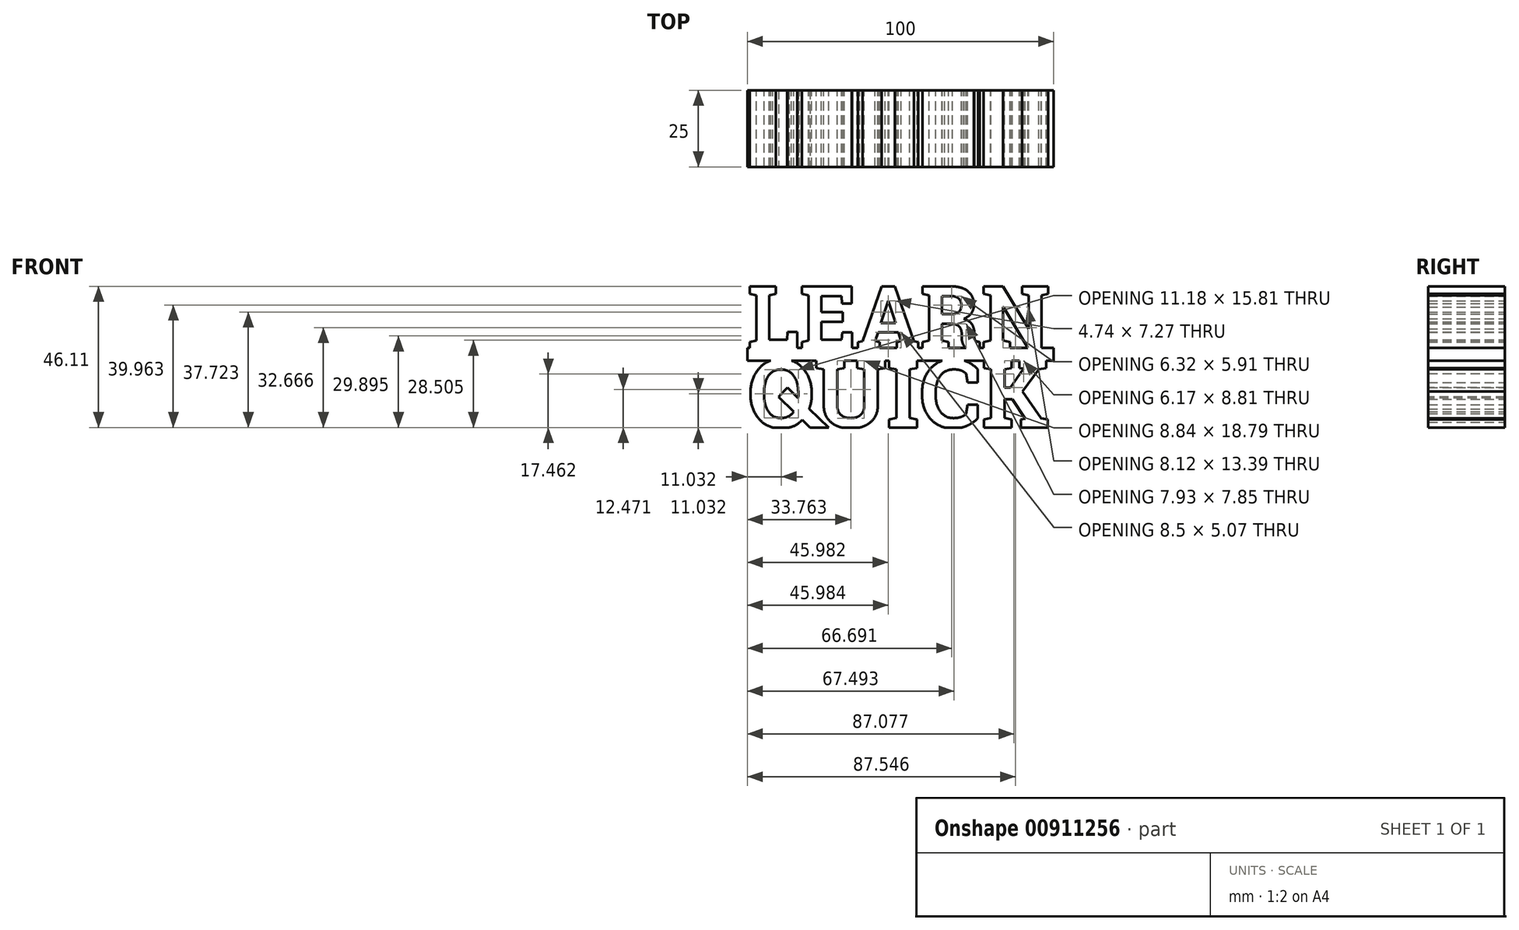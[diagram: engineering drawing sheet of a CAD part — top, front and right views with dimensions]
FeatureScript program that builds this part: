
annotation { "Feature Type Name" : "Feature", "Feature Type Description" : "" }
export const myFeature = defineFeature(function(context is Context, id is Id, definition is map)
    precondition{}
    {
        {
            var Q0;
            Q0=qCreatedBy(makeId("Front.planeOp"),FACE);
            var sketch = newSketch(context, id + "F0", { "sketchPlane" : qUnion([Q0])});
            skText(sketch, "E0", { "text": "LEARN", "fontName": "RobotoSlab-Bold.ttf"});
            skText(sketch, "E1", { "text": "QUICK", "fontName": "RobotoSlab-Bold.ttf"});
            skPoint(sketch, "E2", {"position": v(-50, 0.5) * mm});
            skPoint(sketch, "E3", {"position": v(50, -3.6) * mm});
            skLineSegment(sketch, "E4.bottom", {"start": v(-50, 0.5) * mm, "end": v(50, 0.5) * mm});
            skLineSegment(sketch, "E4.top", {"start": v(-50, -3.6) * mm, "end": v(50, -3.6) * mm});
            skLineSegment(sketch, "E4.left", {"start": v(-50, 0.5) * mm, "end": v(-50, -3.6) * mm});
            skLineSegment(sketch, "E4.right", {"start": v(50, 0.5) * mm, "end": v(50, -3.6) * mm});
            const initialGuessF0  = {"E0": [-0.05, 0, 1, 0, 0.0209], "E1": [-0.05, -0.02547, 1, 0, 0.02236]};
            skSetInitialGuess(sketch, initialGuessF0);
            skSolve(sketch);
        }
        {
            var Q0;
            Q0 = qSketchRegion(id + "F0", true);
            extrude(context, id + "F1", {"entities" : qUnion([Q0]), "depth" : 25 * mm, "offsetDistance" : 25 * mm});
        }
        {
            var Q0;
            Q0=makeQuery(id+"F1.opExtrude","CAP_FACE",FACE,{"disambiguationData":[OSD([sQuery(id+"F0.wireOp",EDGE,"E0.sketch_text.stroke-0"),sQuery(id+"F0.wireOp",EDGE,"E0.sketch_text.stroke-1"),sQuery(id+"F0.wireOp",EDGE,"E0.sketch_text.stroke-2"),sQuery(id+"F0.wireOp",EDGE,"E0.sketch_text.stroke-3"),sQuery(id+"F0.wireOp",EDGE,"E0.sketch_text.stroke-4"),sQuery(id+"F0.wireOp",EDGE,"E0.sketch_text.stroke-5"),sQuery(id+"F0.wireOp",EDGE,"E0.sketch_text.stroke-6"),sQuery(id+"F0.wireOp",EDGE,"E0.sketch_text.stroke-7"),sQuery(id+"F0.wireOp",EDGE,"E0.sketch_text.stroke-8"),sQuery(id+"F0.wireOp",EDGE,"E0.sketch_text.stroke-9"),sQuery(id+"F0.wireOp",EDGE,"E0.sketch_text.stroke-10"),sQuery(id+"F0.wireOp",EDGE,"E0.sketch_text.stroke-11"),sQuery(id+"F0.wireOp",EDGE,"E0.sketch_text.stroke-12"),sQuery(id+"F0.wireOp",EDGE,"E0.sketch_text.stroke-13"),sQuery(id+"F0.wireOp",EDGE,"E0.sketch_text.stroke-14"),sQuery(id+"F0.wireOp",EDGE,"E0.sketch_text.stroke-15"),sQuery(id+"F0.wireOp",EDGE,"E1.sketch_text.stroke-0"),sQuery(id+"F0.wireOp",EDGE,"E1.sketch_text.stroke-1"),sQuery(id+"F0.wireOp",EDGE,"E1.sketch_text.stroke-2"),sQuery(id+"F0.wireOp",EDGE,"E1.sketch_text.stroke-3"),sQuery(id+"F0.wireOp",EDGE,"E1.sketch_text.stroke-4"),sQuery(id+"F0.wireOp",EDGE,"E1.sketch_text.stroke-5"),sQuery(id+"F0.wireOp",EDGE,"E1.sketch_text.stroke-6"),sQuery(id+"F0.wireOp",EDGE,"E1.sketch_text.stroke-7"),sQuery(id+"F0.wireOp",EDGE,"E1.sketch_text.stroke-8"),sQuery(id+"F0.wireOp",EDGE,"E1.sketch_text.stroke-9"),sQuery(id+"F0.wireOp",EDGE,"E1.sketch_text.stroke-10"),sQuery(id+"F0.wireOp",EDGE,"E1.sketch_text.stroke-11"),sQuery(id+"F0.wireOp",EDGE,"E1.sketch_text.stroke-12"),sQuery(id+"F0.wireOp",EDGE,"E1.sketch_text.stroke-13"),sQuery(id+"F0.wireOp",EDGE,"E1.sketch_text.stroke-14"),sQuery(id+"F0.wireOp",EDGE,"E1.sketch_text.stroke-15"),sQuery(id+"F0.wireOp",EDGE,"E1.sketch_text.stroke-16"),sQuery(id+"F0.wireOp",EDGE,"E1.sketch_text.stroke-17"),sQuery(id+"F0.wireOp",EDGE,"E1.sketch_text.stroke-18"),sQuery(id+"F0.wireOp",EDGE,"E1.sketch_text.stroke-19"),sQuery(id+"F0.wireOp",EDGE,"E1.sketch_text.stroke-20"),sQuery(id+"F0.wireOp",EDGE,"E1.sketch_text.stroke-21"),sQuery(id+"F0.wireOp",EDGE,"E1.sketch_text.stroke-22"),sQuery(id+"F0.wireOp",EDGE,"E1.sketch_text.stroke-23"),sQuery(id+"F0.wireOp",EDGE,"E1.sketch_text.stroke-24")])],"isStart":false});
            var sketch = newSketch(context, id + "F2", { "sketchPlane" : qUnion([Q0])});
            skPoint(sketch, "E5", {"position": v(-32.9, -23.74) * mm});
            skPoint(sketch, "E6", {"position": v(-36.63, -25.5) * mm});
            skArc(sketch, "E7", {"start": v(-36.63, -25.5) * mm, "mid": v(-34.64, -24.89) * mm, "end": v(-32.9, -23.74) * mm});
            skLineSegment(sketch, "E8", {"start": v(-36.63, -25.5) * mm, "end": v(-36.63, -30.49) * mm});
            skLineSegment(sketch, "E9", {"start": v(-36.63, -30.49) * mm, "end": v(-26.3, -30.49) * mm});
            skLineSegment(sketch, "E10", {"start": v(-26.3, -30.49) * mm, "end": v(-26.05, -24.24) * mm});
            skLineSegment(sketch, "E11", {"start": v(-26.05, -24.24) * mm, "end": v(-32.9, -23.74) * mm});
            skSolve(sketch);
        }
        {
            var Q0;
            Q0 = qSketchRegion(id + "F2", true);
            extrude(context, id + "F3", {"entities" : qUnion([Q0]), "operationType" : NewBodyOperationType.REMOVE, "endBound" : BoundingType.THROUGH_ALL, "oppositeDirection" : true, "depth" : 25 * mm, "offsetDistance" : 25 * mm});
        }
        {
            var Q0;
            Q0=makeQuery(id+"F1.opExtrude","CAP_FACE",FACE,{"disambiguationData":[OSD([sQuery(id+"F0.wireOp",EDGE,"E0.sketch_text.stroke-0"),sQuery(id+"F0.wireOp",EDGE,"E0.sketch_text.stroke-1"),sQuery(id+"F0.wireOp",EDGE,"E0.sketch_text.stroke-2"),sQuery(id+"F0.wireOp",EDGE,"E0.sketch_text.stroke-3"),sQuery(id+"F0.wireOp",EDGE,"E0.sketch_text.stroke-4"),sQuery(id+"F0.wireOp",EDGE,"E0.sketch_text.stroke-5"),sQuery(id+"F0.wireOp",EDGE,"E0.sketch_text.stroke-6"),sQuery(id+"F0.wireOp",EDGE,"E0.sketch_text.stroke-7"),sQuery(id+"F0.wireOp",EDGE,"E0.sketch_text.stroke-8"),sQuery(id+"F0.wireOp",EDGE,"E0.sketch_text.stroke-9"),sQuery(id+"F0.wireOp",EDGE,"E0.sketch_text.stroke-10"),sQuery(id+"F0.wireOp",EDGE,"E0.sketch_text.stroke-11"),sQuery(id+"F0.wireOp",EDGE,"E0.sketch_text.stroke-12"),sQuery(id+"F0.wireOp",EDGE,"E0.sketch_text.stroke-13"),sQuery(id+"F0.wireOp",EDGE,"E0.sketch_text.stroke-14"),sQuery(id+"F0.wireOp",EDGE,"E0.sketch_text.stroke-15"),sQuery(id+"F0.wireOp",EDGE,"E1.sketch_text.stroke-0"),sQuery(id+"F0.wireOp",EDGE,"E1.sketch_text.stroke-1"),sQuery(id+"F0.wireOp",EDGE,"E1.sketch_text.stroke-2"),sQuery(id+"F0.wireOp",EDGE,"E1.sketch_text.stroke-3"),sQuery(id+"F0.wireOp",EDGE,"E1.sketch_text.stroke-4"),sQuery(id+"F0.wireOp",EDGE,"E1.sketch_text.stroke-5"),sQuery(id+"F0.wireOp",EDGE,"E1.sketch_text.stroke-6"),sQuery(id+"F0.wireOp",EDGE,"E1.sketch_text.stroke-7"),sQuery(id+"F0.wireOp",EDGE,"E1.sketch_text.stroke-8"),sQuery(id+"F0.wireOp",EDGE,"E1.sketch_text.stroke-9"),sQuery(id+"F0.wireOp",EDGE,"E1.sketch_text.stroke-10"),sQuery(id+"F0.wireOp",EDGE,"E1.sketch_text.stroke-11"),sQuery(id+"F0.wireOp",EDGE,"E1.sketch_text.stroke-12"),sQuery(id+"F0.wireOp",EDGE,"E1.sketch_text.stroke-13"),sQuery(id+"F0.wireOp",EDGE,"E1.sketch_text.stroke-14"),sQuery(id+"F0.wireOp",EDGE,"E1.sketch_text.stroke-15"),sQuery(id+"F0.wireOp",EDGE,"E1.sketch_text.stroke-16"),sQuery(id+"F0.wireOp",EDGE,"E1.sketch_text.stroke-17"),sQuery(id+"F0.wireOp",EDGE,"E1.sketch_text.stroke-18"),sQuery(id+"F0.wireOp",EDGE,"E1.sketch_text.stroke-19"),sQuery(id+"F0.wireOp",EDGE,"E1.sketch_text.stroke-20"),sQuery(id+"F0.wireOp",EDGE,"E1.sketch_text.stroke-21"),sQuery(id+"F0.wireOp",EDGE,"E1.sketch_text.stroke-22"),sQuery(id+"F0.wireOp",EDGE,"E1.sketch_text.stroke-23"),sQuery(id+"F0.wireOp",EDGE,"E1.sketch_text.stroke-24")])],"isStart":false});
            var sketch = newSketch(context, id + "F4", { "sketchPlane" : qUnion([Q0])});
            skLineSegment(sketch, "E12", {"start": v(-39.84, -15.45) * mm, "end": v(-29.15, -25.79) * mm});
            skLineSegment(sketch, "E13", {"start": v(-23.15, -25.79) * mm, "end": v(-36.94, -12.45) * mm});
            skLineSegment(sketch, "E14", {"start": v(-29.15, -25.79) * mm, "end": v(-23.15, -25.79) * mm});
            skPoint(sketch, "E15", {"position": v(-39, -25.79) * mm});
            skLineSegment(sketch, "E16", {"start": v(-39, -25.79) * mm, "end": v(-16.24, -25.79) * mm, "construction": true});
            skLineSegment(sketch, "E17", {"start": v(-39.84, -15.45) * mm, "end": v(-36.94, -12.45) * mm});
            skPoint(sketch, "E18.start.orphan", {"position": v(-39, -10.45) * mm});
            skSolve(sketch);
        }
        {
            var Q0;
            Q0 = qSketchRegion(id + "F4", true);
            extrude(context, id + "F5", {"entities" : qUnion([Q0]), "operationType" : NewBodyOperationType.ADD, "oppositeDirection" : true, "depth" : 25 * mm, "offsetDistance" : 25 * mm});
        }
        {
            var Q0;
            Q0=makeQuery(id+"F5.boolean.opBoolean","MERGE",FACE,{"derivedFrom":[makeQuery(id+"F1.opExtrude","CAP_FACE",FACE,{"disambiguationData":[OSD([sQuery(id+"F0.wireOp",EDGE,"E0.sketch_text.stroke-0"),sQuery(id+"F0.wireOp",EDGE,"E0.sketch_text.stroke-1"),sQuery(id+"F0.wireOp",EDGE,"E0.sketch_text.stroke-2"),sQuery(id+"F0.wireOp",EDGE,"E0.sketch_text.stroke-3"),sQuery(id+"F0.wireOp",EDGE,"E0.sketch_text.stroke-4"),sQuery(id+"F0.wireOp",EDGE,"E0.sketch_text.stroke-5"),sQuery(id+"F0.wireOp",EDGE,"E0.sketch_text.stroke-6"),sQuery(id+"F0.wireOp",EDGE,"E0.sketch_text.stroke-7"),sQuery(id+"F0.wireOp",EDGE,"E0.sketch_text.stroke-8"),sQuery(id+"F0.wireOp",EDGE,"E0.sketch_text.stroke-9"),sQuery(id+"F0.wireOp",EDGE,"E0.sketch_text.stroke-10"),sQuery(id+"F0.wireOp",EDGE,"E0.sketch_text.stroke-11"),sQuery(id+"F0.wireOp",EDGE,"E0.sketch_text.stroke-12"),sQuery(id+"F0.wireOp",EDGE,"E0.sketch_text.stroke-13"),sQuery(id+"F0.wireOp",EDGE,"E0.sketch_text.stroke-14"),sQuery(id+"F0.wireOp",EDGE,"E0.sketch_text.stroke-16"),sQuery(id+"F0.wireOp",EDGE,"E0.sketch_text.stroke-17"),sQuery(id+"F0.wireOp",EDGE,"E0.sketch_text.stroke-18"),sQuery(id+"F0.wireOp",EDGE,"E0.sketch_text.stroke-19"),sQuery(id+"F0.wireOp",EDGE,"E0.sketch_text.stroke-20"),sQuery(id+"F0.wireOp",EDGE,"E0.sketch_text.stroke-21"),sQuery(id+"F0.wireOp",EDGE,"E0.sketch_text.stroke-23"),sQuery(id+"F0.wireOp",EDGE,"E0.sketch_text.stroke-24"),sQuery(id+"F0.wireOp",EDGE,"E0.sketch_text.stroke-25"),sQuery(id+"F0.wireOp",EDGE,"E0.sketch_text.stroke-26"),sQuery(id+"F0.wireOp",EDGE,"E0.sketch_text.stroke-27"),sQuery(id+"F0.wireOp",EDGE,"E0.sketch_text.stroke-28"),sQuery(id+"F0.wireOp",EDGE,"E0.sketch_text.stroke-29"),sQuery(id+"F0.wireOp",EDGE,"E0.sketch_text.stroke-30"),sQuery(id+"F0.wireOp",EDGE,"E0.sketch_text.stroke-31"),sQuery(id+"F0.wireOp",EDGE,"E0.sketch_text.stroke-32"),sQuery(id+"F0.wireOp",EDGE,"E0.sketch_text.stroke-33"),sQuery(id+"F0.wireOp",EDGE,"E0.sketch_text.stroke-34"),sQuery(id+"F0.wireOp",EDGE,"E0.sketch_text.stroke-35"),sQuery(id+"F0.wireOp",EDGE,"E0.sketch_text.stroke-36"),sQuery(id+"F0.wireOp",EDGE,"E0.sketch_text.stroke-37"),sQuery(id+"F0.wireOp",EDGE,"E0.sketch_text.stroke-38"),sQuery(id+"F0.wireOp",EDGE,"E0.sketch_text.stroke-39"),sQuery(id+"F0.wireOp",EDGE,"E0.sketch_text.stroke-40"),sQuery(id+"F0.wireOp",EDGE,"E0.sketch_text.stroke-41"),sQuery(id+"F0.wireOp",EDGE,"E0.sketch_text.stroke-42"),sQuery(id+"F0.wireOp",EDGE,"E0.sketch_text.stroke-44"),sQuery(id+"F0.wireOp",EDGE,"E0.sketch_text.stroke-45"),sQuery(id+"F0.wireOp",EDGE,"E0.sketch_text.stroke-46"),sQuery(id+"F0.wireOp",EDGE,"E0.sketch_text.stroke-47"),sQuery(id+"F0.wireOp",EDGE,"E0.sketch_text.stroke-48"),sQuery(id+"F0.wireOp",EDGE,"E0.sketch_text.stroke-49"),sQuery(id+"F0.wireOp",EDGE,"E0.sketch_text.stroke-50"),sQuery(id+"F0.wireOp",EDGE,"E0.sketch_text.stroke-52"),sQuery(id+"F0.wireOp",EDGE,"E0.sketch_text.stroke-53"),sQuery(id+"F0.wireOp",EDGE,"E0.sketch_text.stroke-54"),sQuery(id+"F0.wireOp",EDGE,"E0.sketch_text.stroke-55"),sQuery(id+"F0.wireOp",EDGE,"E0.sketch_text.stroke-56"),sQuery(id+"F0.wireOp",EDGE,"E0.sketch_text.stroke-57"),sQuery(id+"F0.wireOp",EDGE,"E0.sketch_text.stroke-58"),sQuery(id+"F0.wireOp",EDGE,"E0.sketch_text.stroke-59"),sQuery(id+"F0.wireOp",EDGE,"E0.sketch_text.stroke-60"),sQuery(id+"F0.wireOp",EDGE,"E0.sketch_text.stroke-61"),sQuery(id+"F0.wireOp",EDGE,"E0.sketch_text.stroke-62"),sQuery(id+"F0.wireOp",EDGE,"E0.sketch_text.stroke-63"),sQuery(id+"F0.wireOp",EDGE,"E0.sketch_text.stroke-64"),sQuery(id+"F0.wireOp",EDGE,"E0.sketch_text.stroke-65"),sQuery(id+"F0.wireOp",EDGE,"E0.sketch_text.stroke-66"),sQuery(id+"F0.wireOp",EDGE,"E0.sketch_text.stroke-67"),sQuery(id+"F0.wireOp",EDGE,"E0.sketch_text.stroke-69"),sQuery(id+"F0.wireOp",EDGE,"E0.sketch_text.stroke-70"),sQuery(id+"F0.wireOp",EDGE,"E0.sketch_text.stroke-71"),sQuery(id+"F0.wireOp",EDGE,"E0.sketch_text.stroke-72"),sQuery(id+"F0.wireOp",EDGE,"E0.sketch_text.stroke-73"),sQuery(id+"F0.wireOp",EDGE,"E0.sketch_text.stroke-74"),sQuery(id+"F0.wireOp",EDGE,"E0.sketch_text.stroke-75"),sQuery(id+"F0.wireOp",EDGE,"E0.sketch_text.stroke-76"),sQuery(id+"F0.wireOp",EDGE,"E0.sketch_text.stroke-77"),sQuery(id+"F0.wireOp",EDGE,"E0.sketch_text.stroke-79"),sQuery(id+"F0.wireOp",EDGE,"E0.sketch_text.stroke-80"),sQuery(id+"F0.wireOp",EDGE,"E0.sketch_text.stroke-81"),sQuery(id+"F0.wireOp",EDGE,"E0.sketch_text.stroke-82"),sQuery(id+"F0.wireOp",EDGE,"E0.sketch_text.stroke-83"),sQuery(id+"F0.wireOp",EDGE,"E0.sketch_text.stroke-84"),sQuery(id+"F0.wireOp",EDGE,"E0.sketch_text.stroke-85"),sQuery(id+"F0.wireOp",EDGE,"E0.sketch_text.stroke-86"),sQuery(id+"F0.wireOp",EDGE,"E0.sketch_text.stroke-87"),sQuery(id+"F0.wireOp",EDGE,"E0.sketch_text.stroke-88"),sQuery(id+"F0.wireOp",EDGE,"E0.sketch_text.stroke-89"),sQuery(id+"F0.wireOp",EDGE,"E0.sketch_text.stroke-90"),sQuery(id+"F0.wireOp",EDGE,"E0.sketch_text.stroke-91"),sQuery(id+"F0.wireOp",EDGE,"E0.sketch_text.stroke-92"),sQuery(id+"F0.wireOp",EDGE,"E0.sketch_text.stroke-93"),sQuery(id+"F0.wireOp",EDGE,"E0.sketch_text.stroke-94"),sQuery(id+"F0.wireOp",EDGE,"E0.sketch_text.stroke-95"),sQuery(id+"F0.wireOp",EDGE,"E0.sketch_text.stroke-97"),sQuery(id+"F0.wireOp",EDGE,"E0.sketch_text.stroke-98"),sQuery(id+"F0.wireOp",EDGE,"E0.sketch_text.stroke-99"),sQuery(id+"F0.wireOp",EDGE,"E0.sketch_text.stroke-100"),sQuery(id+"F0.wireOp",EDGE,"E0.sketch_text.stroke-101"),sQuery(id+"F0.wireOp",EDGE,"E0.sketch_text.stroke-103"),sQuery(id+"F0.wireOp",EDGE,"E0.sketch_text.stroke-104"),sQuery(id+"F0.wireOp",EDGE,"E0.sketch_text.stroke-105"),sQuery(id+"F0.wireOp",EDGE,"E0.sketch_text.stroke-106"),sQuery(id+"F0.wireOp",EDGE,"E0.sketch_text.stroke-107"),sQuery(id+"F0.wireOp",EDGE,"E0.sketch_text.stroke-108"),sQuery(id+"F0.wireOp",EDGE,"E0.sketch_text.stroke-109"),sQuery(id+"F0.wireOp",EDGE,"E0.sketch_text.stroke-110"),sQuery(id+"F0.wireOp",EDGE,"E0.sketch_text.stroke-111"),sQuery(id+"F0.wireOp",EDGE,"E0.sketch_text.stroke-112"),sQuery(id+"F0.wireOp",EDGE,"E0.sketch_text.stroke-113"),sQuery(id+"F0.wireOp",EDGE,"E0.sketch_text.stroke-114"),sQuery(id+"F0.wireOp",EDGE,"E0.sketch_text.stroke-115"),sQuery(id+"F0.wireOp",EDGE,"E0.sketch_text.stroke-116"),sQuery(id+"F0.wireOp",EDGE,"E1.sketch_text.stroke-0"),sQuery(id+"F0.wireOp",EDGE,"E1.sketch_text.stroke-1"),sQuery(id+"F0.wireOp",EDGE,"E1.sketch_text.stroke-2"),sQuery(id+"F0.wireOp",EDGE,"E1.sketch_text.stroke-3"),sQuery(id+"F0.wireOp",EDGE,"E1.sketch_text.stroke-4"),sQuery(id+"F0.wireOp",EDGE,"E1.sketch_text.stroke-5"),sQuery(id+"F0.wireOp",EDGE,"E1.sketch_text.stroke-6"),sQuery(id+"F0.wireOp",EDGE,"E1.sketch_text.stroke-7"),sQuery(id+"F0.wireOp",EDGE,"E1.sketch_text.stroke-8"),sQuery(id+"F0.wireOp",EDGE,"E1.sketch_text.stroke-9"),sQuery(id+"F0.wireOp",EDGE,"E1.sketch_text.stroke-10"),sQuery(id+"F0.wireOp",EDGE,"E1.sketch_text.stroke-11"),sQuery(id+"F0.wireOp",EDGE,"E1.sketch_text.stroke-12"),sQuery(id+"F0.wireOp",EDGE,"E1.sketch_text.stroke-13"),sQuery(id+"F0.wireOp",EDGE,"E1.sketch_text.stroke-14"),sQuery(id+"F0.wireOp",EDGE,"E1.sketch_text.stroke-15"),sQuery(id+"F0.wireOp",EDGE,"E1.sketch_text.stroke-16"),sQuery(id+"F0.wireOp",EDGE,"E1.sketch_text.stroke-17"),sQuery(id+"F0.wireOp",EDGE,"E1.sketch_text.stroke-18"),sQuery(id+"F0.wireOp",EDGE,"E1.sketch_text.stroke-19"),sQuery(id+"F0.wireOp",EDGE,"E1.sketch_text.stroke-20"),sQuery(id+"F0.wireOp",EDGE,"E1.sketch_text.stroke-21"),sQuery(id+"F0.wireOp",EDGE,"E1.sketch_text.stroke-22"),sQuery(id+"F0.wireOp",EDGE,"E1.sketch_text.stroke-23"),sQuery(id+"F0.wireOp",EDGE,"E1.sketch_text.stroke-24"),sQuery(id+"F0.wireOp",EDGE,"E1.sketch_text.stroke-25"),sQuery(id+"F0.wireOp",EDGE,"E1.sketch_text.stroke-26"),sQuery(id+"F0.wireOp",EDGE,"E1.sketch_text.stroke-27"),sQuery(id+"F0.wireOp",EDGE,"E1.sketch_text.stroke-28"),sQuery(id+"F0.wireOp",EDGE,"E1.sketch_text.stroke-29"),sQuery(id+"F0.wireOp",EDGE,"E1.sketch_text.stroke-30"),sQuery(id+"F0.wireOp",EDGE,"E1.sketch_text.stroke-31"),sQuery(id+"F0.wireOp",EDGE,"E1.sketch_text.stroke-32"),sQuery(id+"F0.wireOp",EDGE,"E1.sketch_text.stroke-33"),sQuery(id+"F0.wireOp",EDGE,"E1.sketch_text.stroke-34"),sQuery(id+"F0.wireOp",EDGE,"E1.sketch_text.stroke-36"),sQuery(id+"F0.wireOp",EDGE,"E1.sketch_text.stroke-37"),sQuery(id+"F0.wireOp",EDGE,"E1.sketch_text.stroke-38"),sQuery(id+"F0.wireOp",EDGE,"E1.sketch_text.stroke-39"),sQuery(id+"F0.wireOp",EDGE,"E1.sketch_text.stroke-40"),sQuery(id+"F0.wireOp",EDGE,"E1.sketch_text.stroke-41"),sQuery(id+"F0.wireOp",EDGE,"E1.sketch_text.stroke-42"),sQuery(id+"F0.wireOp",EDGE,"E1.sketch_text.stroke-43"),sQuery(id+"F0.wireOp",EDGE,"E1.sketch_text.stroke-44"),sQuery(id+"F0.wireOp",EDGE,"E1.sketch_text.stroke-45"),sQuery(id+"F0.wireOp",EDGE,"E1.sketch_text.stroke-49"),sQuery(id+"F0.wireOp",EDGE,"E1.sketch_text.stroke-51"),sQuery(id+"F0.wireOp",EDGE,"E1.sketch_text.stroke-52"),sQuery(id+"F0.wireOp",EDGE,"E1.sketch_text.stroke-53"),sQuery(id+"F0.wireOp",EDGE,"E1.sketch_text.stroke-54"),sQuery(id+"F0.wireOp",EDGE,"E1.sketch_text.stroke-55"),sQuery(id+"F0.wireOp",EDGE,"E1.sketch_text.stroke-56"),sQuery(id+"F0.wireOp",EDGE,"E1.sketch_text.stroke-57"),sQuery(id+"F0.wireOp",EDGE,"E1.sketch_text.stroke-58"),sQuery(id+"F0.wireOp",EDGE,"E1.sketch_text.stroke-59"),sQuery(id+"F0.wireOp",EDGE,"E1.sketch_text.stroke-60"),sQuery(id+"F0.wireOp",EDGE,"E1.sketch_text.stroke-61"),sQuery(id+"F0.wireOp",EDGE,"E1.sketch_text.stroke-62"),sQuery(id+"F0.wireOp",EDGE,"E1.sketch_text.stroke-63"),sQuery(id+"F0.wireOp",EDGE,"E1.sketch_text.stroke-64"),sQuery(id+"F0.wireOp",EDGE,"E1.sketch_text.stroke-65"),sQuery(id+"F0.wireOp",EDGE,"E1.sketch_text.stroke-66"),sQuery(id+"F0.wireOp",EDGE,"E1.sketch_text.stroke-67"),sQuery(id+"F0.wireOp",EDGE,"E1.sketch_text.stroke-68"),sQuery(id+"F0.wireOp",EDGE,"E1.sketch_text.stroke-69"),sQuery(id+"F0.wireOp",EDGE,"E1.sketch_text.stroke-70"),sQuery(id+"F0.wireOp",EDGE,"E1.sketch_text.stroke-71"),sQuery(id+"F0.wireOp",EDGE,"E1.sketch_text.stroke-72"),sQuery(id+"F0.wireOp",EDGE,"E1.sketch_text.stroke-73"),sQuery(id+"F0.wireOp",EDGE,"E1.sketch_text.stroke-74"),sQuery(id+"F0.wireOp",EDGE,"E1.sketch_text.stroke-75"),sQuery(id+"F0.wireOp",EDGE,"E1.sketch_text.stroke-76"),sQuery(id+"F0.wireOp",EDGE,"E1.sketch_text.stroke-77"),sQuery(id+"F0.wireOp",EDGE,"E1.sketch_text.stroke-78"),sQuery(id+"F0.wireOp",EDGE,"E1.sketch_text.stroke-79"),sQuery(id+"F0.wireOp",EDGE,"E1.sketch_text.stroke-80"),sQuery(id+"F0.wireOp",EDGE,"E1.sketch_text.stroke-81"),sQuery(id+"F0.wireOp",EDGE,"E1.sketch_text.stroke-82"),sQuery(id+"F0.wireOp",EDGE,"E1.sketch_text.stroke-83"),sQuery(id+"F0.wireOp",EDGE,"E1.sketch_text.stroke-84"),sQuery(id+"F0.wireOp",EDGE,"E1.sketch_text.stroke-85"),sQuery(id+"F0.wireOp",EDGE,"E1.sketch_text.stroke-86"),sQuery(id+"F0.wireOp",EDGE,"E1.sketch_text.stroke-87"),sQuery(id+"F0.wireOp",EDGE,"E1.sketch_text.stroke-88"),sQuery(id+"F0.wireOp",EDGE,"E1.sketch_text.stroke-90"),sQuery(id+"F0.wireOp",EDGE,"E1.sketch_text.stroke-91"),sQuery(id+"F0.wireOp",EDGE,"E1.sketch_text.stroke-92"),sQuery(id+"F0.wireOp",EDGE,"E1.sketch_text.stroke-93"),sQuery(id+"F0.wireOp",EDGE,"E1.sketch_text.stroke-94"),sQuery(id+"F0.wireOp",EDGE,"E1.sketch_text.stroke-95"),sQuery(id+"F0.wireOp",EDGE,"E1.sketch_text.stroke-96"),sQuery(id+"F0.wireOp",EDGE,"E1.sketch_text.stroke-98"),sQuery(id+"F0.wireOp",EDGE,"E1.sketch_text.stroke-99"),sQuery(id+"F0.wireOp",EDGE,"E1.sketch_text.stroke-100"),sQuery(id+"F0.wireOp",EDGE,"E1.sketch_text.stroke-101"),sQuery(id+"F0.wireOp",EDGE,"E1.sketch_text.stroke-102"),sQuery(id+"F0.wireOp",EDGE,"E1.sketch_text.stroke-103"),sQuery(id+"F0.wireOp",EDGE,"E1.sketch_text.stroke-104"),sQuery(id+"F0.wireOp",EDGE,"E1.sketch_text.stroke-105"),sQuery(id+"F0.wireOp",EDGE,"E1.sketch_text.stroke-106"),sQuery(id+"F0.wireOp",EDGE,"E1.sketch_text.stroke-107"),sQuery(id+"F0.wireOp",EDGE,"E1.sketch_text.stroke-108"),sQuery(id+"F0.wireOp",EDGE,"E1.sketch_text.stroke-109"),sQuery(id+"F0.wireOp",EDGE,"E1.sketch_text.stroke-110"),sQuery(id+"F0.wireOp",EDGE,"E1.sketch_text.stroke-111"),sQuery(id+"F0.wireOp",EDGE,"E1.sketch_text.stroke-112"),sQuery(id+"F0.wireOp",EDGE,"E1.sketch_text.stroke-113"),sQuery(id+"F0.wireOp",EDGE,"E4.bottom"),sQuery(id+"F0.wireOp",EDGE,"E4.top"),sQuery(id+"F0.wireOp",EDGE,"E4.left"),sQuery(id+"F0.wireOp",EDGE,"E4.right")])],"isStart":false}),makeQuery(id+"F5.opExtrude","CAP_FACE",FACE,{"disambiguationData":[OSD([sQuery(id+"F4.wireOp",EDGE,"E12"),sQuery(id+"F4.wireOp",EDGE,"E13"),sQuery(id+"F4.wireOp",EDGE,"E18"),sQuery(id+"F4.wireOp",EDGE,"E14")])],"isStart":true})]});
            var sketch = newSketch(context, id + "F6", { "sketchPlane" : qUnion([Q0])});
            skLineSegment(sketch, "E19", {"start": v(0.68, -25.47) * mm, "end": v(57.48, -25.47) * mm});
            skLineSegment(sketch, "E20", {"start": v(57.48, -25.47) * mm, "end": v(57.48, -39.63) * mm});
            skLineSegment(sketch, "E21", {"start": v(57.48, -39.63) * mm, "end": v(-52.35, -39.63) * mm});
            skLineSegment(sketch, "E22", {"start": v(-52.35, -39.63) * mm, "end": v(-52.35, -25.47) * mm});
            skLineSegment(sketch, "E23", {"start": v(-52.35, -25.47) * mm, "end": v(0.68, -25.47) * mm});
            skSolve(sketch);
        }
        {
            var Q0;
            Q0 = qSketchRegion(id + "F6", true);
            extrude(context, id + "F7", {"entities" : qUnion([Q0]), "operationType" : NewBodyOperationType.REMOVE, "endBound" : BoundingType.THROUGH_ALL, "oppositeDirection" : true, "depth" : 25 * mm, "offsetDistance" : 25 * mm});
        }
    });
